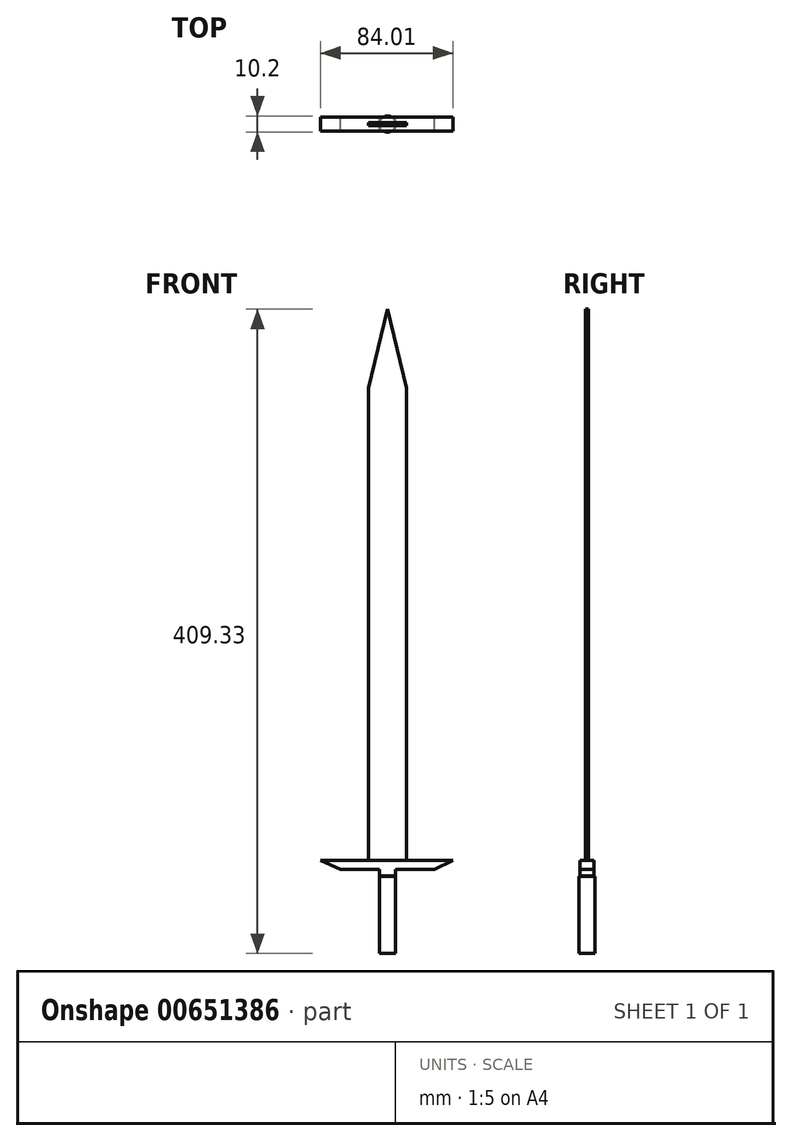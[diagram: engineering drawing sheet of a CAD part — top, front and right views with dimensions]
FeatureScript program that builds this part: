
annotation { "Feature Type Name" : "Feature", "Feature Type Description" : "" }
export const myFeature = defineFeature(function(context is Context, id is Id, definition is map)
    precondition{}
    {
        {
            var Q0;
            Q0=qCreatedBy(makeId("Front.planeOp"),FACE);
            var sketch = newSketch(context, id + "F0", { "sketchPlane" : qUnion([Q0])});
            skArc(sketch, "E0", {"start": v(0, -75.35) * mm, "mid": v(8.55, -69.92) * mm, "end": v(0, -64.49) * mm});
            skLineSegment(sketch, "E1", {"start": v(0, -64.49) * mm, "end": v(5.1, -64.49) * mm});
            skLineSegment(sketch, "E2", {"start": v(5.1, -64.49) * mm, "end": v(5.1, -15.49) * mm});
            skLineSegment(sketch, "E3", {"start": v(5.1, -15.49) * mm, "end": v(0, -15.49) * mm});
            skLineSegment(sketch, "E4", {"start": v(0, -15.49) * mm, "end": v(0, -64.49) * mm});
            skLineSegment(sketch, "E5", {"start": v(0, -15.49) * mm, "end": v(0, -75.35) * mm});
            skSolve(sketch);
        }
        {
            var Q0;
            Q0 = qSketchRegion(id + "F0", true);
            var Q1;
            Q1=sQuery(id+"F0.wireOp",EDGE,"E5");
            revolve(context, id + "F1", {"entities" : qUnion([Q0]), "axis" : qUnion([Q1]), "revolveType" : RevolveType.FULL});
        }
        {
            var Q0;
            Q0=qCreatedBy(makeId("Front.planeOp"),FACE);
            var sketch = newSketch(context, id + "F2", { "sketchPlane" : qUnion([Q0])});
            skLineSegment(sketch, "E6", {"start": v(-5.17, -15.18) * mm, "end": v(-5.17, -10.9) * mm});
            skLineSegment(sketch, "E7", {"start": v(-5.17, -10.9) * mm, "end": v(-30, -10.9) * mm});
            skLineSegment(sketch, "E8", {"start": v(-5.17, -15.18) * mm, "end": v(4.86, -15.18) * mm});
            skLineSegment(sketch, "E9", {"start": v(4.86, -15.18) * mm, "end": v(4.86, -10.9) * mm});
            skLineSegment(sketch, "E10", {"start": v(4.86, -10.9) * mm, "end": v(29.68, -10.9) * mm});
            skLineSegment(sketch, "E11", {"start": v(29.68, -10.9) * mm, "end": v(41.43, -5.24) * mm});
            skLineSegment(sketch, "E12", {"start": v(41.43, -5.24) * mm, "end": v(-42.58, -5.24) * mm});
            skLineSegment(sketch, "E13", {"start": v(-42.58, -5.24) * mm, "end": v(-30, -10.9) * mm});
            skSolve(sketch);
        }
        {
            var Q0;
            Q0 = qSketchRegion(id + "F2", true);
            extrude(context, id + "F3", {"entities" : qUnion([Q0]), "depth" : 4.5 * mm, "offsetDistance" : 25 * mm, "hasSecondDirection" : true, "secondDirectionOppositeDirection" : true, "secondDirectionDepth" : 4.5 * mm});
        }
        {
            var Q0;
            Q0=qCreatedBy(makeId("Front.planeOp"),FACE);
            var sketch = newSketch(context, id + "F4", { "sketchPlane" : qUnion([Q0])});
            skLineSegment(sketch, "E14", {"start": v(0, -5.16) * mm, "end": v(0, 344.84) * mm});
            skLineSegment(sketch, "E15", {"start": v(0, -5.16) * mm, "end": v(-12, -5.16) * mm});
            skLineSegment(sketch, "E16", {"start": v(0, -5.16) * mm, "end": v(12, -5.16) * mm});
            skLineSegment(sketch, "E17", {"start": v(12, -5.16) * mm, "end": v(12, 294.84) * mm});
            skLineSegment(sketch, "E18", {"start": v(-12, 294.84) * mm, "end": v(-12, -5.16) * mm});
            skLineSegment(sketch, "E19", {"start": v(12, 294.84) * mm, "end": v(0, 344.84) * mm});
            skLineSegment(sketch, "E20", {"start": v(-12, 294.84) * mm, "end": v(0, 344.84) * mm});
            skSolve(sketch);
        }
        {
            var Q0;
            Q0 = qSketchRegion(id + "F4", true);
            extrude(context, id + "F5", {"entities" : qUnion([Q0]), "depth" : 1 * mm, "offsetDistance" : 25 * mm, "hasSecondDirection" : true, "secondDirectionOppositeDirection" : true, "secondDirectionDepth" : 1 * mm});
        }
    });
